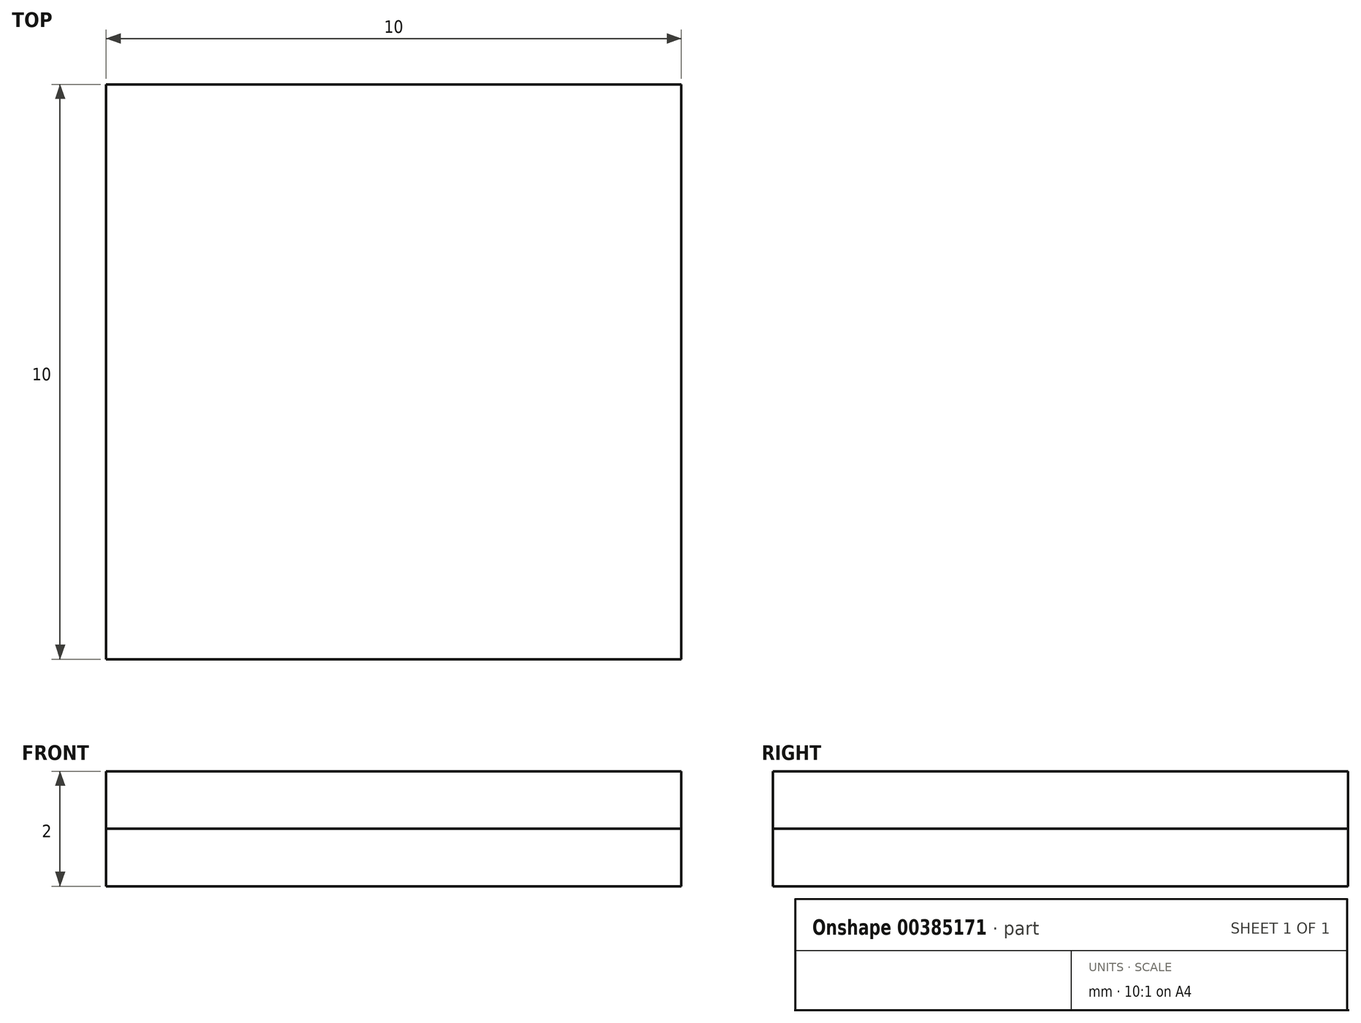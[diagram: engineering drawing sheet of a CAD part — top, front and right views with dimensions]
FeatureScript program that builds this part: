
annotation { "Feature Type Name" : "Feature", "Feature Type Description" : "" }
export const myFeature = defineFeature(function(context is Context, id is Id, definition is map)
    precondition{}
    {
        {
            var Q0;
            Q0=qCreatedBy(makeId("Top.planeOp"),FACE);
            var sketch = newSketch(context, id + "F0", { "sketchPlane" : qUnion([Q0])});
            skLineSegment(sketch, "E0.bottom", {"start": v(0, 3.1) * mm, "end": v(10, 3.1) * mm});
            skLineSegment(sketch, "E0.top", {"start": v(0, -6.9) * mm, "end": v(10, -6.9) * mm});
            skLineSegment(sketch, "E0.left", {"start": v(0, 3.1) * mm, "end": v(0, -6.9) * mm});
            skLineSegment(sketch, "E0.right", {"start": v(10, 3.1) * mm, "end": v(10, -6.9) * mm});
            skPoint(sketch, "E1.firstSnap0", {"position": v(0, -1.9) * mm});
            skSolve(sketch);
        }
        {
            var Q0;
            Q0 = qSketchRegion(id + "F0", true);
            extrude(context, id + "F1", {"entities" : qUnion([Q0]), "depth" : 1 * mm});
        }
        {
            var Q0;
            Q0=makeQuery(id+"F1.opExtrude","CAP_FACE",FACE,{"disambiguationData":[OSD([sQuery(id+"F0.wireOp",EDGE,"E0.bottom"),sQuery(id+"F0.wireOp",EDGE,"E0.top"),sQuery(id+"F0.wireOp",EDGE,"E0.left"),sQuery(id+"F0.wireOp",EDGE,"E0.right")])],"isStart":false});
            extrude(context, id + "F2", {"entities" : qUnion([Q0]), "depth" : 1 * mm});
        }
    });
